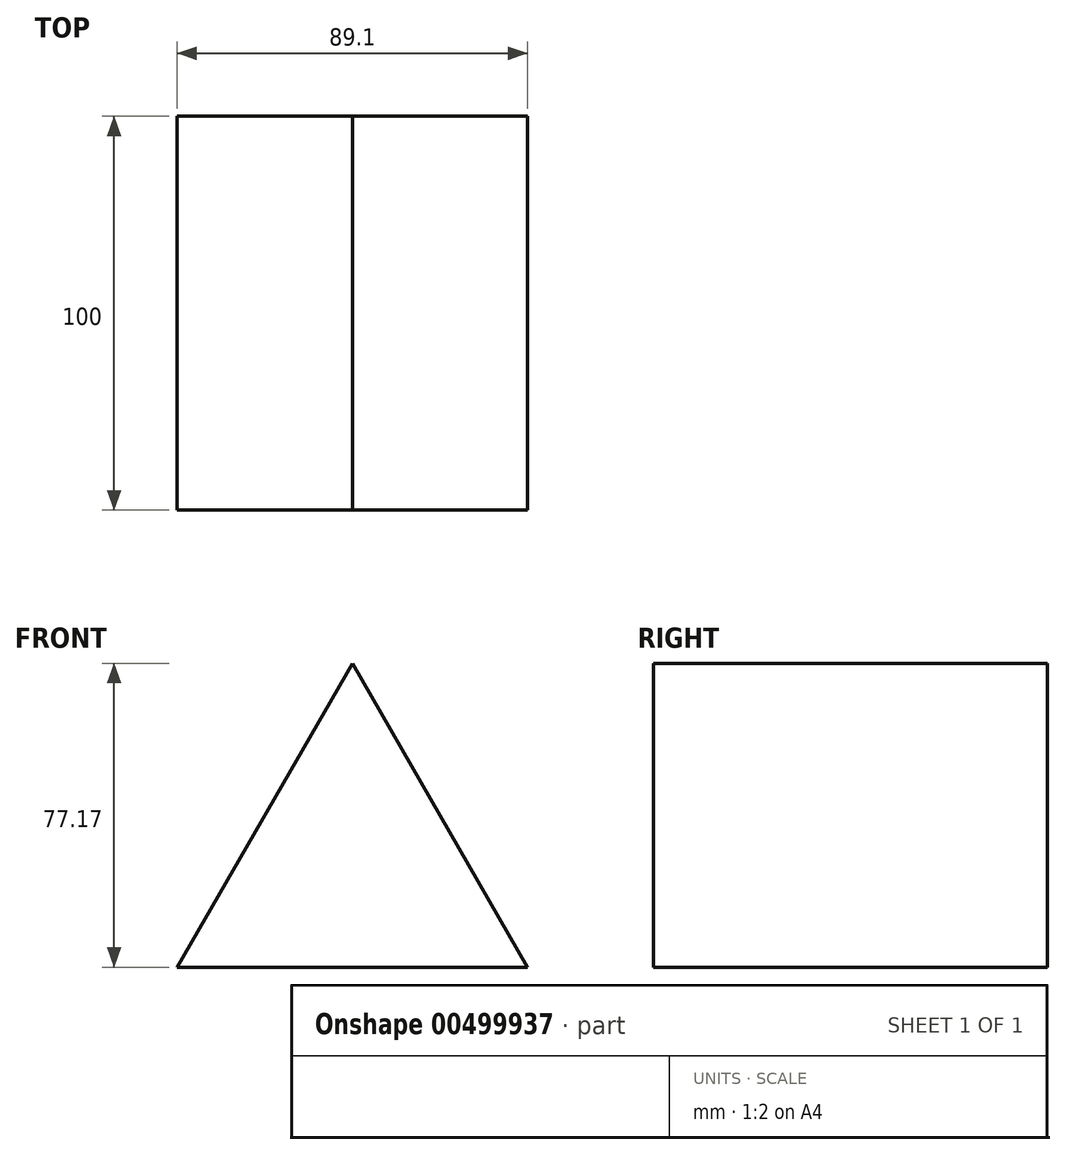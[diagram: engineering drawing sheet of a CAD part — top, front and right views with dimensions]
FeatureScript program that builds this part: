
annotation { "Feature Type Name" : "Feature", "Feature Type Description" : "" }
export const myFeature = defineFeature(function(context is Context, id is Id, definition is map)
    precondition{}
    {
        {
            var Q0;
            Q0=qCreatedBy(makeId("Front.planeOp"),FACE);
            var sketch = newSketch(context, id + "F0", { "sketchPlane" : qUnion([Q0])});
            skCircle(sketch, "E0.cCircle", {"center": v(0, 0) * mm, "radius": 51.45 * mm, "construction": true});
            skLineSegment(sketch, "E0.0", {"start": v(0, 51.45) * mm, "end": v(44.55, -25.72) * mm});
            skLineSegment(sketch, "E0.1", {"start": v(44.55, -25.72) * mm, "end": v(-44.55, -25.72) * mm});
            skLineSegment(sketch, "E0.2", {"start": v(-44.55, -25.72) * mm, "end": v(0, 51.45) * mm});
            skSolve(sketch);
        }
        {
            var Q0;
            Q0=makeQuery(id+"F0.imprint","IMPRINT",FACE,{"disambiguationData":[TD([[makeQuery(id+"F0.imprint","IMPRINT",EDGE,{"derivedFrom":sQuery(id+"F0.wireOp",EDGE,"E0.0")}),-1.0]])]});
            extrude(context, id + "F1", {"entities" : qUnion([Q0]), "depth" : 100 * mm});
        }
    });
